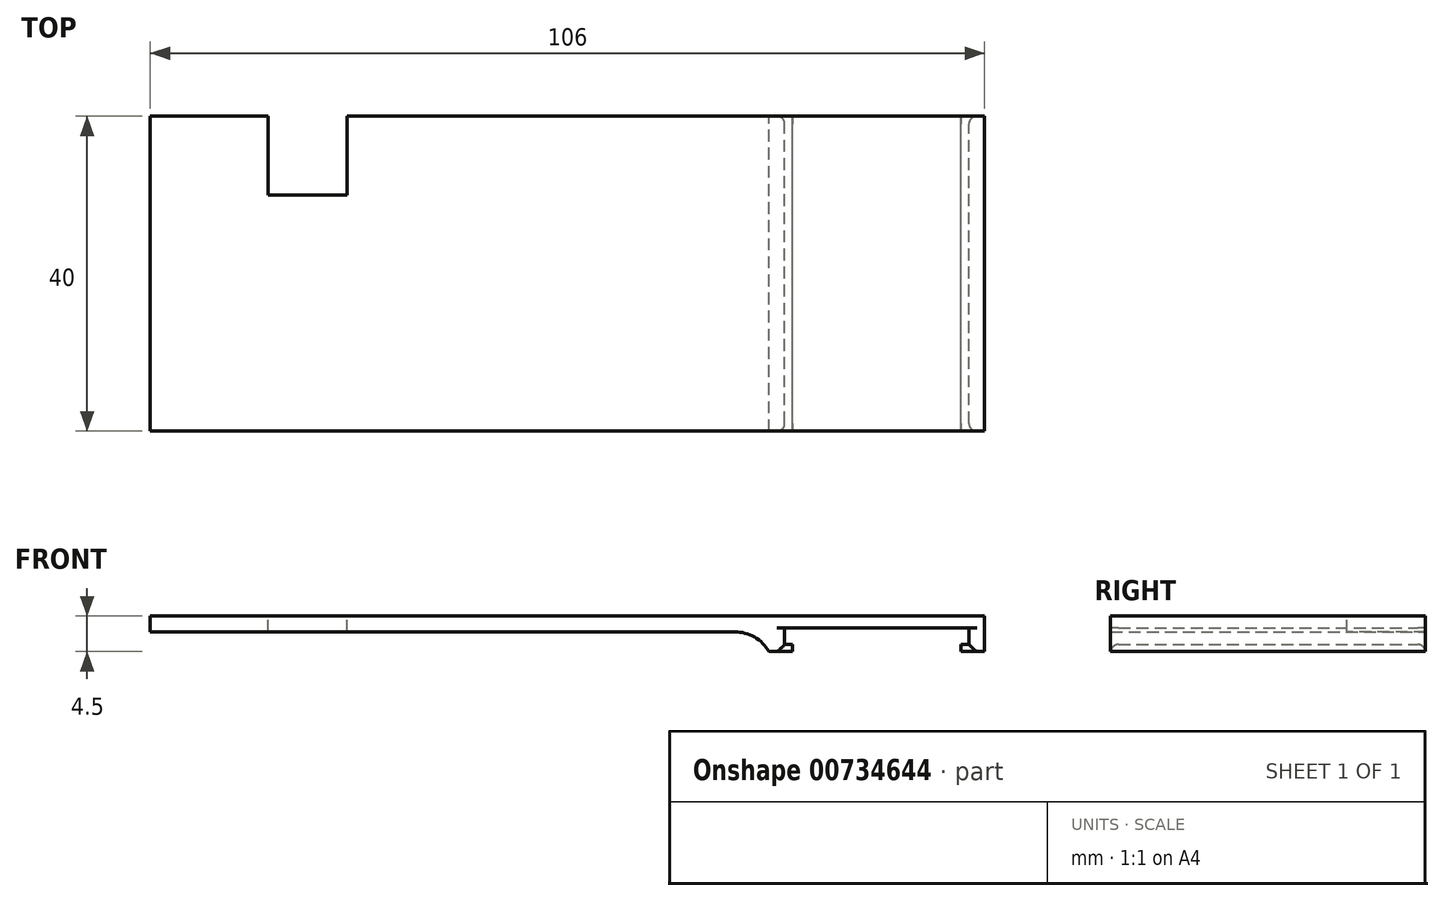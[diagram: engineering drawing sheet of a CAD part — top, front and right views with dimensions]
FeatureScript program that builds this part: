
annotation { "Feature Type Name" : "Feature", "Feature Type Description" : "" }
export const myFeature = defineFeature(function(context is Context, id is Id, definition is map)
    precondition{}
    {
        {
            var Q0;
            Q0=qCreatedBy(makeId("Front.planeOp"),FACE);
            var sketch = newSketch(context, id + "F0", { "sketchPlane" : qUnion([Q0])});
            skLineSegment(sketch, "E0.bottom", {"start": v(0, 0) * mm, "end": v(106, 0) * mm});
            skLineSegment(sketch, "E0.top", {"start": v(0, -2) * mm, "end": v(78.6, -2) * mm});
            skLineSegment(sketch, "E0.left", {"start": v(0, 0) * mm, "end": v(0, -2) * mm});
            skLineSegment(sketch, "E0.right", {"start": v(106, 0) * mm, "end": v(106, -2) * mm});
            skLineSegment(sketch, "E1.top", {"start": v(106, -4.5) * mm, "end": v(103, -4.5) * mm});
            skLineSegment(sketch, "E1.left", {"start": v(106, -2) * mm, "end": v(106, -4.5) * mm});
            skLineSegment(sketch, "E1.right", {"start": v(103, -3.6) * mm, "end": v(103, -4.5) * mm});
            skLineSegment(sketch, "E2", {"start": v(103, -3.6) * mm, "end": v(104, -3.6) * mm});
            skLineSegment(sketch, "E3", {"start": v(104, -3.6) * mm, "end": v(104, -2) * mm});
            skLineSegment(sketch, "E4.top", {"start": v(78.6, -4.5) * mm, "end": v(81.6, -4.5) * mm});
            skLineSegment(sketch, "E4.left", {"start": v(78.6, -2) * mm, "end": v(78.6, -4.5) * mm});
            skLineSegment(sketch, "E4.right", {"start": v(81.6, -3.6) * mm, "end": v(81.6, -4.5) * mm});
            skLineSegment(sketch, "E5", {"start": v(81.6, -3.6) * mm, "end": v(80.6, -3.6) * mm});
            skLineSegment(sketch, "E6", {"start": v(80.6, -3.6) * mm, "end": v(80.6, -2) * mm});
            skLineSegment(sketch, "E7", {"start": v(104, -2) * mm, "end": v(104, -1.5) * mm});
            skLineSegment(sketch, "E8", {"start": v(80.6, -1.5) * mm, "end": v(80.6, -2) * mm});
            skLineSegment(sketch, "E9", {"start": v(80.6, -1.5) * mm, "end": v(104, -1.5) * mm});
            skSolve(sketch);
        }
        {
            var Q0;
            Q0 = qSketchRegion(id + "F0", true);
            extrude(context, id + "F1", {"entities" : qUnion([Q0]), "depth" : 40 * mm, "offsetDistance" : 25 * mm});
        }
        {
            var Q0;
            Q0=makeQuery(id+"F1.opExtrude","SWEPT_EDGE",EDGE,{"disambiguationData":[OSD([sQuery(id+"F0.wireOp",EDGE,"E0.top"),sQuery(id+"F0.wireOp",EDGE,"E4.left")])]});
            fillet(context, id + "F2", {"entities" : qUnion([Q0]), "tangentPropagation" : true, "radius" : 5 * mm, "defaultsChanged" : false, "vertexSettings" : [], "allowEdgeOverflow" : false});
        }
        {
            var Q0;
            Q0=makeQuery(id+"F1.opExtrude","CAP_EDGE",EDGE,{"disambiguationData":[OSD([sQuery(id+"F0.wireOp",EDGE,"E6")])],"isStart":false});
            var Q1;
            Q1=makeQuery(id+"F1.opExtrude","CAP_EDGE",EDGE,{"disambiguationData":[OSD([sQuery(id+"F0.wireOp",EDGE,"E3")])],"isStart":false});
            var Q2;
            Q2=makeQuery(id+"F1.opExtrude","CAP_EDGE",EDGE,{"disambiguationData":[OSD([sQuery(id+"F0.wireOp",EDGE,"E6")])],"isStart":true});
            var Q3;
            Q3=makeQuery(id+"F1.opExtrude","CAP_EDGE",EDGE,{"disambiguationData":[OSD([sQuery(id+"F0.wireOp",EDGE,"E3")])],"isStart":true});
            var Q4;
            Q4=makeQuery(id+"F1.opExtrude","CAP_EDGE",EDGE,{"disambiguationData":[OSD([sQuery(id+"F0.wireOp",EDGE,"E5")])],"isStart":true});
            var Q5;
            Q5=makeQuery(id+"F1.opExtrude","CAP_EDGE",EDGE,{"disambiguationData":[OSD([sQuery(id+"F0.wireOp",EDGE,"E2")])],"isStart":true});
            var Q6;
            Q6=makeQuery(id+"F1.opExtrude","CAP_EDGE",EDGE,{"disambiguationData":[OSD([sQuery(id+"F0.wireOp",EDGE,"E5")])],"isStart":false});
            var Q7;
            Q7=makeQuery(id+"F1.opExtrude","CAP_EDGE",EDGE,{"disambiguationData":[OSD([sQuery(id+"F0.wireOp",EDGE,"E2")])],"isStart":false});
            fillet(context, id + "F3", {"entities" : qUnion([Q0, Q1, Q2, Q3, Q4, Q5, Q6, Q7]), "tangentPropagation" : true, "radius" : 1 * mm, "defaultsChanged" : false, "vertexSettings" : [], "allowEdgeOverflow" : false});
        }
        {
            var Q0;
            Q0=makeQuery(id+"F1.opExtrude","SWEPT_FACE",FACE,{"disambiguationData":[OSD([sQuery(id+"F0.wireOp",EDGE,"E0.bottom")])]});
            var sketch = newSketch(context, id + "F4", { "sketchPlane" : qUnion([Q0])});
            skLineSegment(sketch, "E10.bottom", {"start": v(15, 0) * mm, "end": v(25, 0) * mm});
            skLineSegment(sketch, "E10.top", {"start": v(15, -10) * mm, "end": v(25, -10) * mm});
            skLineSegment(sketch, "E10.left", {"start": v(15, 0) * mm, "end": v(15, -10) * mm});
            skLineSegment(sketch, "E10.right", {"start": v(25, 0) * mm, "end": v(25, -10) * mm});
            skSolve(sketch);
        }
        {
            var Q0;
            Q0 = qSketchRegion(id + "F4", true);
            extrude(context, id + "F5", {"entities" : qUnion([Q0]), "operationType" : NewBodyOperationType.REMOVE, "endBound" : BoundingType.THROUGH_ALL, "oppositeDirection" : true, "depth" : 25 * mm, "offsetDistance" : 25 * mm});
        }
    });
